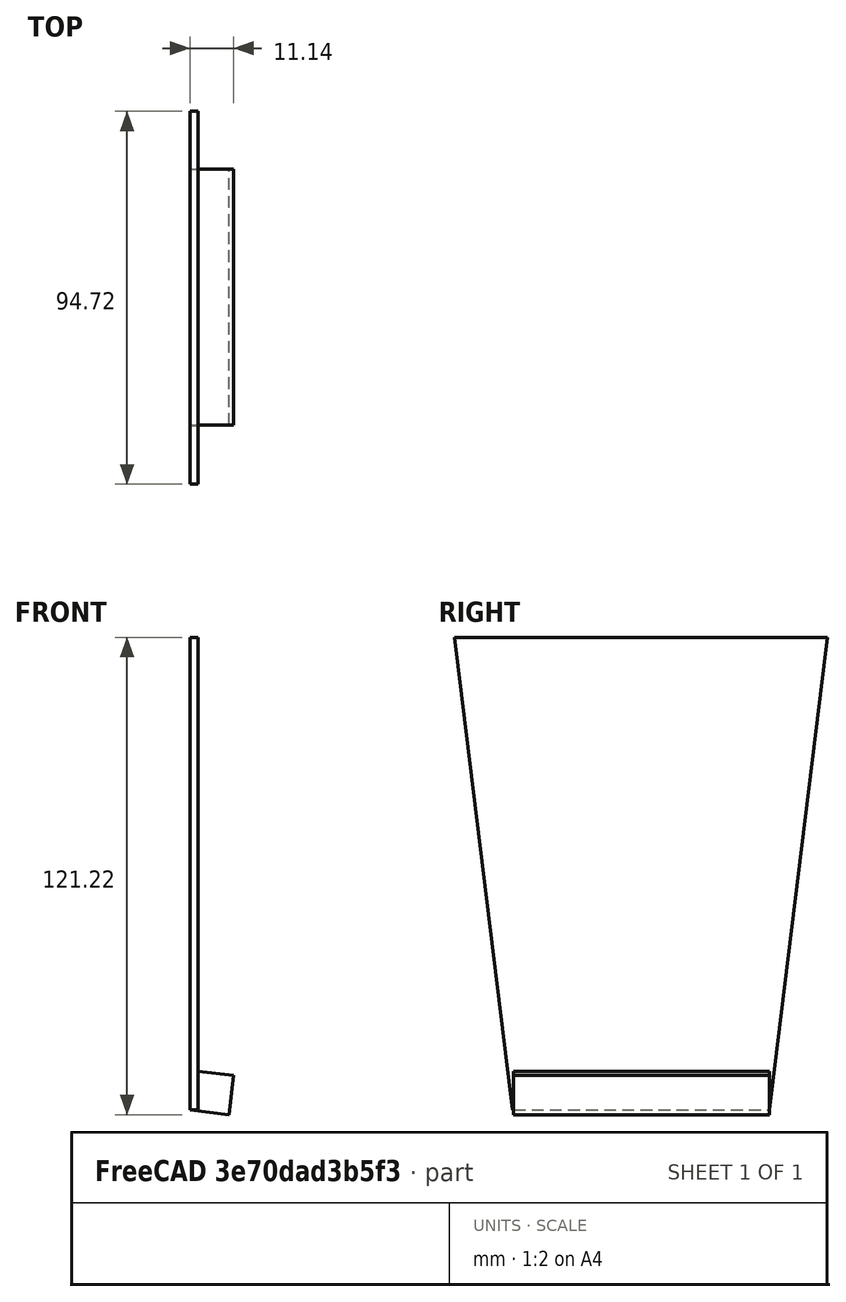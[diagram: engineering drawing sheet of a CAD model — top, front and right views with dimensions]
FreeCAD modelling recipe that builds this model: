
FCSTD DOCUMENT  (FreeCAD 0.14R3702 (Git))
Label: vertical_face_mark2
License: CC-BY 3.0
LicenseURL: http://creativecommons.org/licenses/by/3.0/
objects: Part::Box×4, Part::Cut×2, Part::MultiFuse×1
note: 7 computed .brp shape members not serialized (recipe doc carries the construction recipe); baked Part::Feature solids carry a one-line shape summary decoded from their .brp

FEATURE [Part::Box] Box  label="Cube"
  Height = 120
  Length = 2
  Width = 95
FEATURE [Part::Box] Box001  label="Cube001"
  Height = 140
  Length = 10
  Placement = pos=(0,0,-3) rot=(1,0,0;0.122173rad)
  Width = 15
FEATURE [Part::Box] Box002  label="Cube002"
  Height = 140
  Length = 10
  Placement = pos=(0,80,0) rot=(-1,0,0;0.122173rad)
  Width = 15
FEATURE [Part::Cut] Cut
  Base = -> Box
  Tool = -> Box001
FEATURE [Part::Cut] Cut001
  Base = -> Cut
  Tool = -> Box002
FEATURE [Part::Box] Box004  label="Cube004"
  Height = 10
  Length = 10
  Placement = pos=(0,15,0) rot=(0,1,0;0.122173rad)
  Width = 65
FEATURE [Part::MultiFuse] Fusion
  Shapes = -> [Box004,Cut001]
